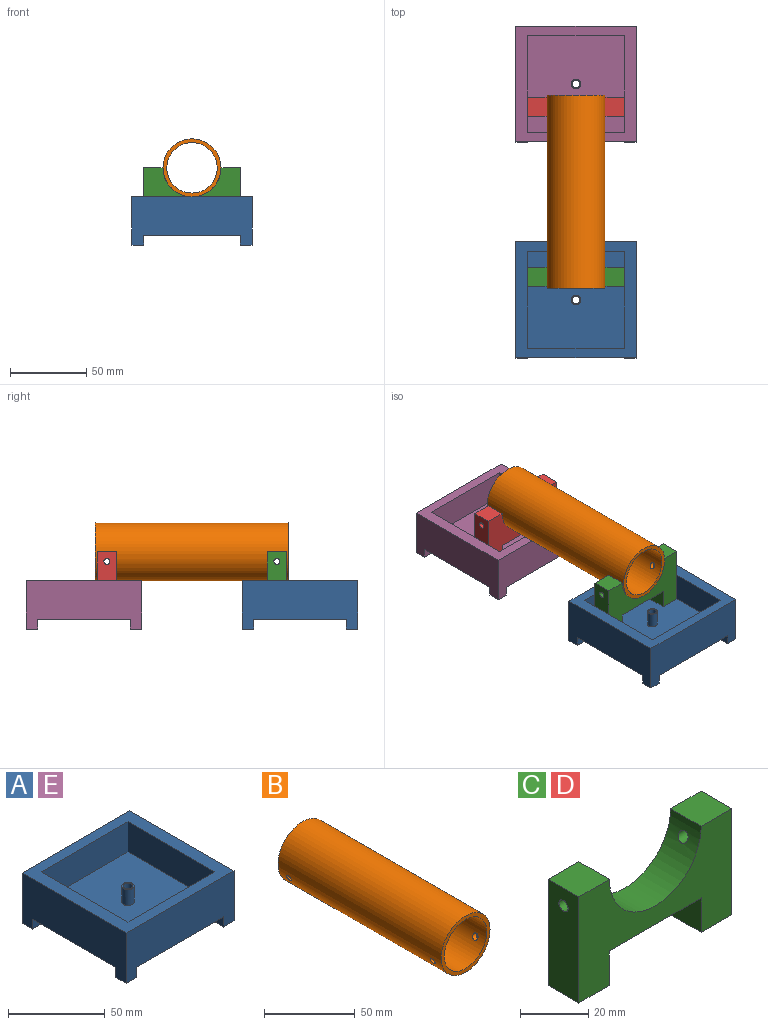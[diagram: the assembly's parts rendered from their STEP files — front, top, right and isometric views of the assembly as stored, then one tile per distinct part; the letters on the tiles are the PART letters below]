
ASSEMBLY  parts=5 mates=6
PART A: 26 faces, bbox 78.9x76.2x31.8 mm
  f0: plane 63.5x19.05mm, normal (0,-1,0), area 1209.7mm2, adj f1,f7,f8,f10
  f1: plane 63.5x19.05mm, normal (-1,0,0), area 1209.7mm2, adj f0,f2,f8,f10
  f2: plane 63.5x19.05mm, normal (0,1,0), area 1209.7mm2, adj f1,f7,f8,f10
  f3: plane 76.2x31.75mm, normal (1,0,0), area 2032.3mm2, adj f4,f6,f8,f9,f21,f22,f23,f25
  f4: plane 78.9x31.75mm, normal (0,1,0), area 2100.9mm2, adj f3,f5,f8,f9,f18,f19,f24,f25
  f5: plane 76.2x31.75mm, normal (-1,0,0), area 2032.3mm2, adj f4,f6,f8,f9,f14,f16,f17,f19
  f6: plane 78.9x31.75mm, normal (0,-1,0), area 2100.9mm2, adj f3,f5,f8,f9,f15,f16,f20,f22
  f7: plane 63.5x19.05mm, normal (1,0,0), area 1209.7mm2, adj f0,f2,f8,f10
  f8: plane 78.9x76.2mm, normal (0,0,1), area 1980.1mm2, adj f0,f1,f2,f3,f4,f5,f6,f7
  f9: plane 78.9x76.2mm, normal (0,0,-1), area 5760.6mm2, adj f3,f4,f5,f6,f13,f14,f15,f17
  f10: plane 63.5x63.5mm, normal (0,0,1), area 4000.6mm2, adj f0,f1,f2,f7,f11
  f11: cylinder r=3.17mm len=10.16mm, axis (0,0,-1), area 202.7mm2, adj f10,f12
  f12: plane 6.35x6.35mm, normal (0,0,1), area 12.2mm2, adj f11,f13
  f13: cylinder r=2.49mm len=16.51mm, axis (0,0,1), area 258.4mm2, adj f9,f12
  f14: plane 7.62x6.35mm, normal (0,1,0), area 48.4mm2, adj f5,f9,f15,f16
  f15: plane 7.62x6.35mm, normal (1,0,0), area 48.4mm2, adj f6,f9,f14,f16
  f16: plane 7.62x7.62mm, normal (0,0,-1), area 58.1mm2, adj f5,f6,f14,f15
  f17: plane 7.62x6.35mm, normal (0,-1,0), area 48.4mm2, adj f5,f9,f18,f19
  f18: plane 7.62x6.35mm, normal (1,0,0), area 48.4mm2, adj f4,f9,f17,f19
  f19: plane 7.62x7.62mm, normal (0,0,-1), area 58.1mm2, adj f4,f5,f17,f18
  f20: plane 7.62x6.35mm, normal (-1,0,0), area 48.4mm2, adj f6,f9,f21,f22
  f21: plane 7.62x6.35mm, normal (0,1,0), area 48.4mm2, adj f3,f9,f20,f22
  f22: plane 7.62x7.62mm, normal (0,0,-1), area 58.1mm2, adj f3,f6,f20,f21
  f23: plane 7.62x6.35mm, normal (0,-1,0), area 48.4mm2, adj f3,f9,f24,f25
  f24: plane 7.62x6.35mm, normal (-1,0,0), area 48.4mm2, adj f4,f9,f23,f25
  f25: plane 7.62x7.62mm, normal (0,0,-1), area 58.1mm2, adj f3,f4,f23,f24
PART B: 8 faces, bbox 38.1x127x38.1 mm
  f0: cylinder r=19.05mm len=127mm, axis (0,1,0), area 15152.6mm2, adj f1,f2,f4,f5,f6,f7
  f1: plane 38.1x38.1mm, normal (0,-1,0), area 278mm2, adj f0,f3
  f2: plane 38.1x38.1mm, normal (0,1,0), area 278mm2, adj f0,f3
  f3: cylinder r=16.57mm len=127mm, axis (0,-1,0), area 13168.8mm2, adj f1,f2,f4,f5,f6,f7
  f4: cylinder r=1.91mm len=4.16mm, axis (1,0,0), area 32mm2, adj f0,f3
  f5: cylinder r=1.91mm len=4.16mm, axis (1,0,0), area 32mm2, adj f0,f3
  f6: cylinder r=1.91mm len=4.16mm, axis (1,0,0), area 32mm2, adj f0,f3
  f7: cylinder r=1.91mm len=4.16mm, axis (1,0,0), area 32mm2, adj f0,f3
PART C: 14 faces, bbox 63.5x12.7x38.1 mm
  f0: plane 12.7x12.35mm, normal (-1,0,0), area 156.9mm2, adj f1,f9,f10,f11
  f1: plane 12.7x12.7mm, normal (0,0,-1), area 161.3mm2, adj f0,f2,f10,f11
  f2: plane 38.1x12.7mm, normal (1,0,0), area 472.5mm2, adj f1,f3,f10,f11,f13
  f3: plane 12.7x12.7mm, normal (0,0,1), area 161.3mm2, adj f2,f4,f10,f11
  f4: cylinder r=19.05mm len=38.1mm, axis (0,1,0), area 735.7mm2, adj f3,f5,f10,f11,f12,f13
  f5: plane 12.7x12.7mm, normal (0,0,1), area 161.3mm2, adj f4,f6,f10,f11
  f6: plane 38.1x12.7mm, normal (-1,0,0), area 472.5mm2, adj f5,f7,f10,f11,f12
  f7: plane 12.7x12.7mm, normal (0,0,-1), area 161.3mm2, adj f6,f8,f10,f11
  f8: plane 12.7x12.35mm, normal (1,0,0), area 156.9mm2, adj f7,f9,f10,f11
  f9: plane 38.1x12.7mm, normal (0,0,-1), area 483.9mm2, adj f0,f8,f10,f11
  f10: plane 63.5x38.1mm, normal (0,-1,0), area 1378.6mm2, adj f0,f1,f2,f3,f4,f5,f6,f7
  f11: plane 63.5x38.1mm, normal (0,1,0), area 1378.6mm2, adj f0,f1,f2,f3,f4,f5,f6,f7
  f12: cylinder r=1.91mm len=14.58mm, axis (-1,0,0), area 165.7mm2, adj f4,f6
  f13: cylinder r=1.91mm len=14.58mm, axis (-1,0,0), area 165.7mm2, adj f2,f4
PART D: same geometry as C
PART E: same geometry as A
PLACE A t=(56.41,-12.95,-65.53)mm
PLACE B t=(56.41,121.68,-21.08)mm
PLACE C t=(56.41,8.64,-21.08)mm
PLACE D t=(56.41,120.41,-21.08)mm
PLACE E t=(56.41,129.05,-65.53)mm
MATE slider B.f0 <-> D.f4  axis (0,1,0) through (56.41,58.18,-21.08)mm
MATE planar E.f1 <-> D.f2  axis (-1,0,0) through (88.16,129.05,-49.65)mm
MATE planar E.f11 <-> D.f1  axis (0,0,1) through (56.41,129.05,-59.18)mm
MATE planar A.f11 <-> C.f7  axis (0,0,1) through (56.41,-12.95,-59.18)mm
MATE planar C.f6 <-> A.f7  axis (-1,0,0) through (24.66,-4.06,-40.13)mm
MATE slider B.f0 <-> C.f4  axis (0,1,0) through (56.41,58.18,-21.08)mm
